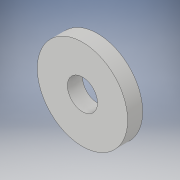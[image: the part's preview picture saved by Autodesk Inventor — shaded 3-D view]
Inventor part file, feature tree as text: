
AUTODESK INVENTOR PART (.ipt)
format: ipt  version: 2018 (Build 220112000, 112)  size: 97,280 bytes
history: native  units: in
note: dims shown in document units (in); Inventor stores cm internally (conversion verified against a paired STEP export)
features: extrude x1, sketch x1
ambient origin geometry x8: Origin, YZ Plane, XZ Plane, XY Plane, X Axis, Y Axis, Z Axis, Center Point
bodies: Solid1 (feature_tree)
feature tree (2):
  extrude  "Extrusion1"  Depth=0.125in
  sketch  "Sketch1"  dims[d0=0.75in d1=0.25in d2=0.125in d3=0.0in]
